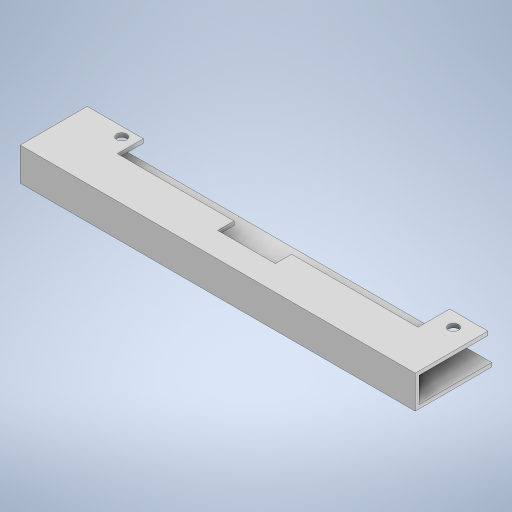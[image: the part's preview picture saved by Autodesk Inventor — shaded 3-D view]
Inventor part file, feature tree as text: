
AUTODESK INVENTOR PART (.ipt)
format: ipt  version: 2024 (Build 280153000, 153)  size: 280,064 bytes
history: native  units: in
note: dims shown in document units (in); Inventor stores cm internally (conversion verified against a paired STEP export)
features: extrude x4, sketch x1
ambient origin geometry x8: Origin, YZ Plane, XZ Plane, XY Plane, X Axis, Y Axis, Z Axis, Center Point
bodies: Solid1 (feature_tree)
feature tree (5):
  sketch  "Sketch1"  dims[d0=0.1043in d1=0.1043in d2=4.0591in d3=0.5768in d4=0.3937in d5=0.7087in d6=0.6496in d7=0.5541in d8=0.4498in d9=0.3839in d10=0.564in d11=0.2096in d12=0.0394in d13=0.0in d14=0.0394in d15=0.2992in d16=0.0in d17=0.0394in d18=0.748in d19=0.0in d21=0.5906in d23=0.0787in d24=0.0in d25=1.2992in d26=0.2559in]
  extrude  "Extrusion1"  Depth=0.2559in
  extrude  "Extrusion2"  Depth=4.0591in
  extrude  "Extrusion3"  Depth=0.5768in
  extrude  "Extrusion4"  Depth=0.3937in
